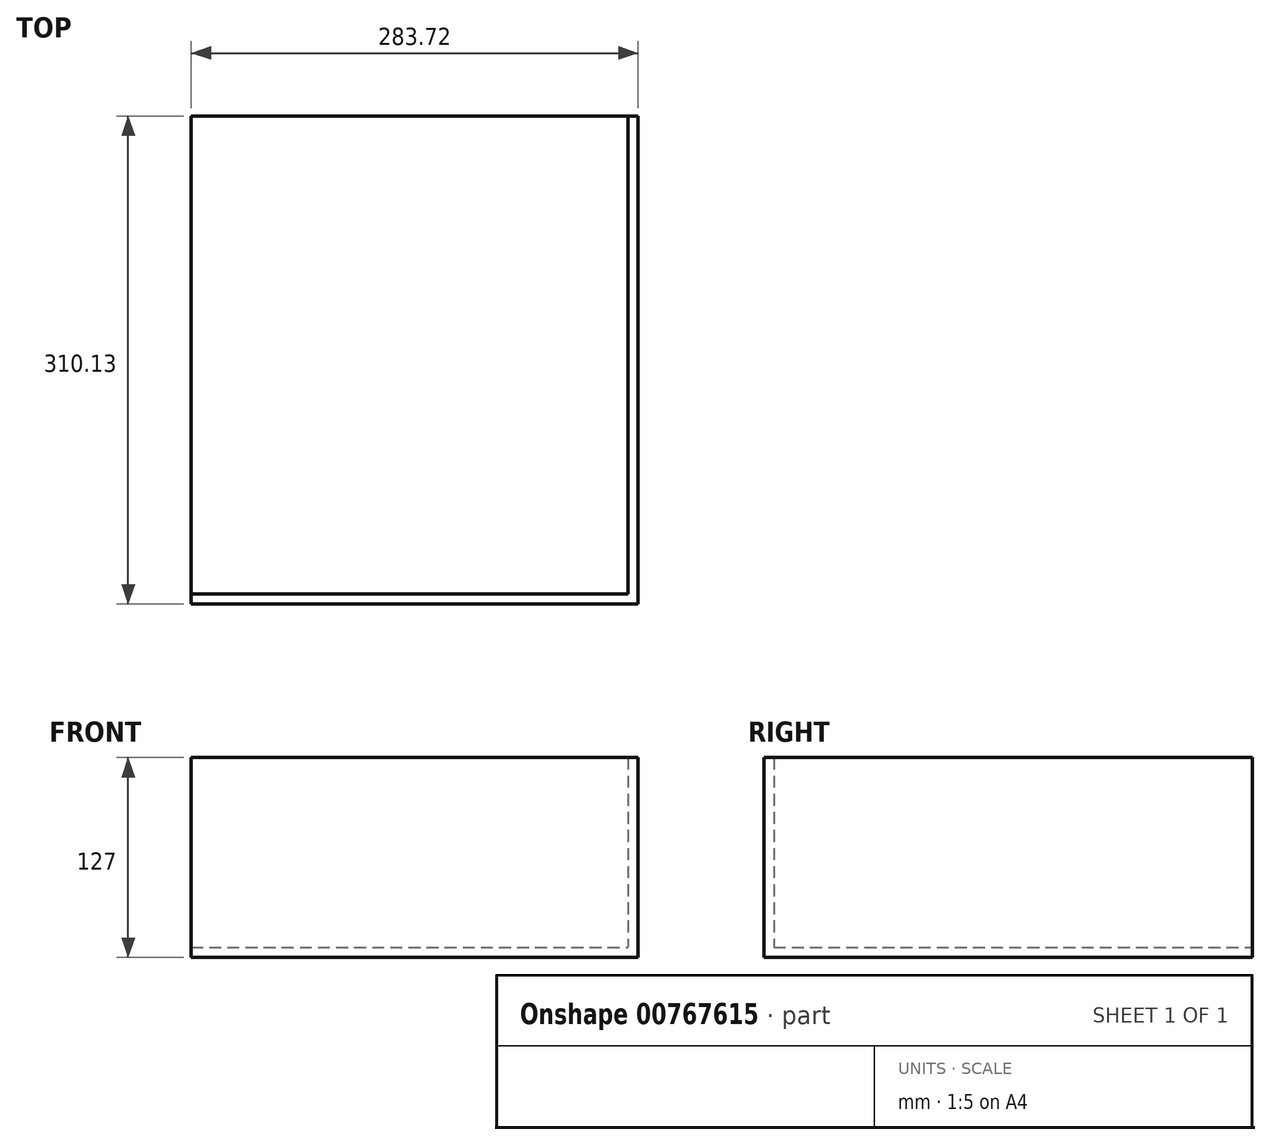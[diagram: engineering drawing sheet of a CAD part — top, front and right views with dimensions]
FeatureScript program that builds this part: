
annotation { "Feature Type Name" : "Feature", "Feature Type Description" : "" }
export const myFeature = defineFeature(function(context is Context, id is Id, definition is map)
    precondition{}
    {
        {
            var Q0;
            Q0=qCreatedBy(makeId("Top.planeOp"),FACE);
            var sketch = newSketch(context, id + "F0", { "sketchPlane" : qUnion([Q0])});
            skLineSegment(sketch, "E0.bottom", {"start": v(0, 0) * mm, "end": v(277.37, 0) * mm});
            skLineSegment(sketch, "E0.top", {"start": v(0, 303.78) * mm, "end": v(277.37, 303.78) * mm});
            skLineSegment(sketch, "E0.left", {"start": v(0, 0) * mm, "end": v(0, 303.78) * mm});
            skLineSegment(sketch, "E0.right", {"start": v(277.37, 0) * mm, "end": v(277.37, 303.78) * mm});
            skSolve(sketch);
        }
        {
            var Q0;
            Q0=makeQuery(id+"F0.imprint","IMPRINT",FACE,{"disambiguationData":[TD([[makeQuery(id+"F0.imprint","IMPRINT",EDGE,{"derivedFrom":sQuery(id+"F0.wireOp",EDGE,"E0.bottom")}),1.0]])]});
            extrude(context, id + "F1", {"entities" : qUnion([Q0]), "depth" : 6.35 * mm, "offsetDistance" : 25.4 * mm});
        }
        {
            var Q0;
            Q0=makeQuery(id+"F1.opExtrude","SWEPT_FACE",FACE,{"disambiguationData":[OSD([sQuery(id+"F0.wireOp",EDGE,"E0.bottom")])]});
            var sketch = newSketch(context, id + "F2", { "sketchPlane" : qUnion([Q0])});
            skLineSegment(sketch, "E1.bottom", {"start": v(277.37, 0) * mm, "end": v(0, 0) * mm});
            skLineSegment(sketch, "E1.top", {"start": v(277.37, 127) * mm, "end": v(0, 127) * mm});
            skLineSegment(sketch, "E1.left", {"start": v(277.37, 0) * mm, "end": v(277.37, 127) * mm});
            skLineSegment(sketch, "E1.right", {"start": v(0, 0) * mm, "end": v(0, 127) * mm});
            skSolve(sketch);
        }
        {
            var Q0;
            Q0 = qSketchRegion(id + "F2", true);
            var Q1;
            {var subQ0=sQuery(id+"F2.wireOp",EDGE,"E1.top");Q1=makeQuery(id+"F2.imprint","IMPRINT",FACE,{"disambiguationData":[TD([[makeQuery(id+"F2.imprint","IMPRINT",EDGE,{"derivedFrom":subQ0}),1.0]])]});}
            extrude(context, id + "F3", {"entities" : qUnion([Q0, Q1]), "operationType" : NewBodyOperationType.ADD, "depth" : 6.35 * mm, "offsetDistance" : 25.4 * mm});
        }
        {
            var Q0;
            Q0=makeQuery(id+"F3.boolean.opBoolean","MERGE",FACE,{"derivedFrom":[makeQuery(id+"F1.opExtrude","SWEPT_FACE",FACE,{"disambiguationData":[OSD([sQuery(id+"F0.wireOp",EDGE,"E0.right")])]}),makeQuery(id+"F3.opExtrude","SWEPT_FACE",FACE,{"disambiguationData":[OSD([sQuery(id+"F2.wireOp",EDGE,"E1.left")])]})]});
            var sketch = newSketch(context, id + "F4", { "sketchPlane" : qUnion([Q0])});
            skLineSegment(sketch, "E2.bottom", {"start": v(-6.35, 0) * mm, "end": v(303.78, 0) * mm});
            skLineSegment(sketch, "E2.top", {"start": v(-6.35, 127) * mm, "end": v(303.78, 127) * mm});
            skLineSegment(sketch, "E2.left", {"start": v(-6.35, 0) * mm, "end": v(-6.35, 127) * mm});
            skLineSegment(sketch, "E2.right", {"start": v(303.78, 0) * mm, "end": v(303.78, 127) * mm});
            skSolve(sketch);
        }
        {
            var Q0;
            Q0 = qSketchRegion(id + "F4", true);
            var Q1;
            {var subQ4=makeQuery(id+"F1.opExtrude","CAP_EDGE",EDGE,{"disambiguationData":[OSD([sQuery(id+"F0.wireOp",EDGE,"E0.right")])],"isStart":false});Q1=makeQuery(id+"F4.imprint","IMPRINT",FACE,{"disambiguationData":[TD([[makeQuery(id+"F4.imprint","IMPRINT",EDGE,{"derivedFrom":subQ4}),1.0]])]});}
            extrude(context, id + "F5", {"entities" : qUnion([Q0, Q1]), "operationType" : NewBodyOperationType.ADD, "depth" : 6.35 * mm, "offsetDistance" : 25.4 * mm});
        }
    });
